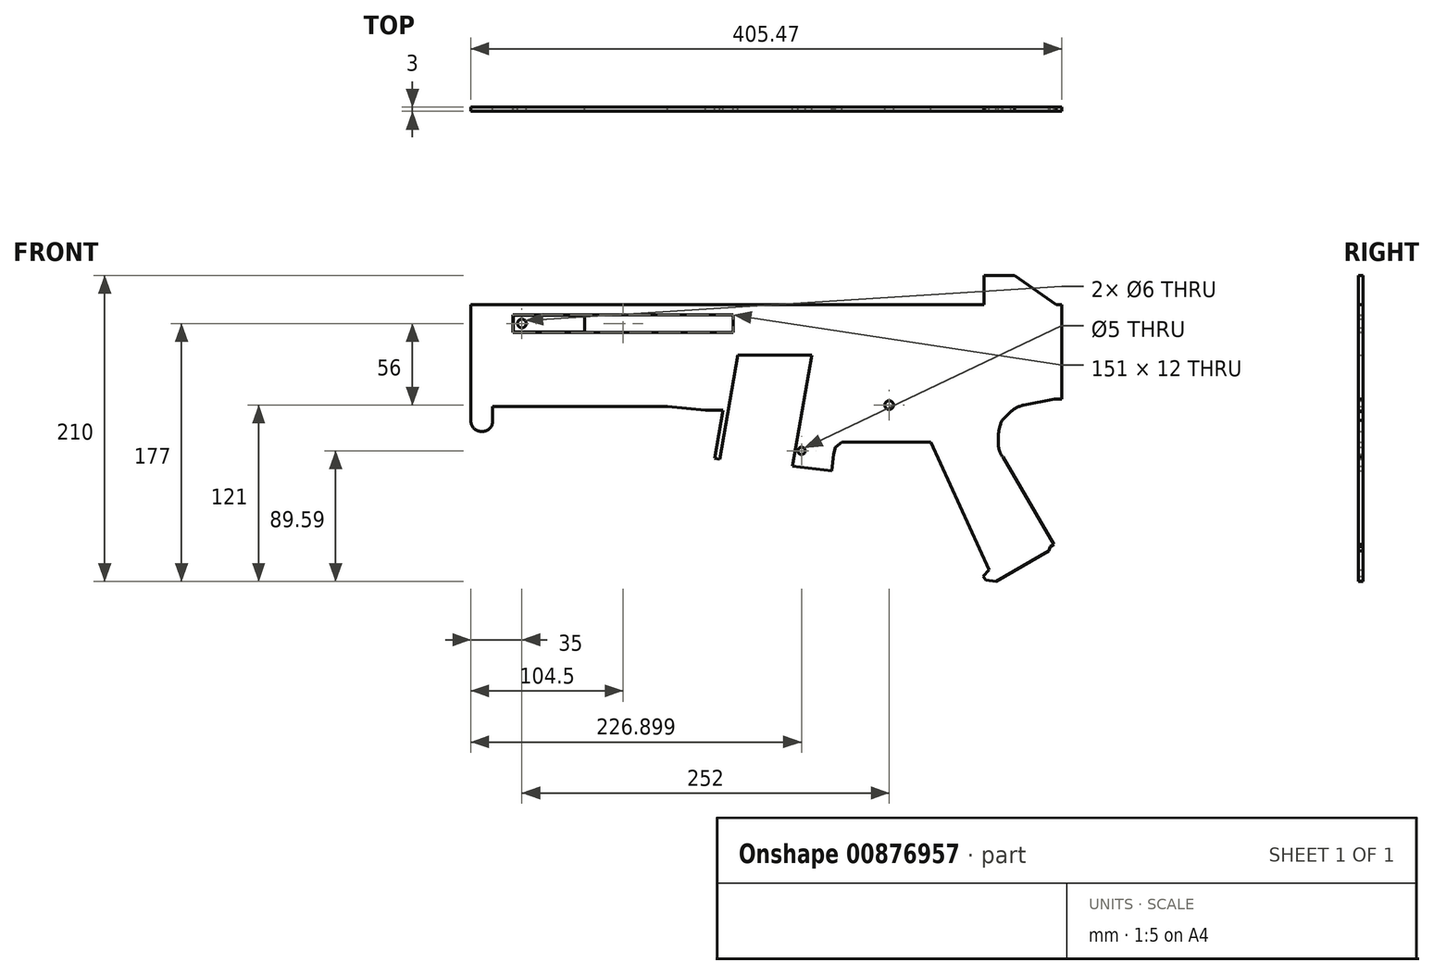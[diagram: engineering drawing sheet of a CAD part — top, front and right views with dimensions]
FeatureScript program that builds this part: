
annotation { "Feature Type Name" : "Feature", "Feature Type Description" : "" }
export const myFeature = defineFeature(function(context is Context, id is Id, definition is map)
    precondition{}
    {
        {
            var Q0;
            Q0=qCreatedBy(makeId("Front.planeOp"),FACE);
            var sketch = newSketch(context, id + "F0", { "sketchPlane" : qUnion([Q0])});
            skLineSegment(sketch, "E0", {"start": v(53.47, -65) * mm, "end": v(53.47, 0) * mm});
            skLineSegment(sketch, "E1", {"start": v(0, 0) * mm, "end": v(-0.03, 20) * mm});
            skLineSegment(sketch, "E2", {"start": v(-0.03, 20) * mm, "end": v(20.97, 20) * mm});
            skPoint(sketch, "E3.visualSharp", {"position": v(-0.03, 20) * mm});
            skPoint(sketch, "E4.visualSharp", {"position": v(20.97, 20) * mm});
            skPoint(sketch, "E5.visualSharp", {"position": v(53.47, 0) * mm});
            skPoint(sketch, "E6.visualSharp", {"position": v(0, 0) * mm});
            skLineSegment(sketch, "E7", {"start": v(53.47, -65) * mm, "end": v(48.47, -65) * mm});
            skLineSegment(sketch, "E8", {"start": v(48.47, -65) * mm, "end": v(27.47, -69) * mm});
            skLineSegment(sketch, "E9", {"start": v(18.47, -73.5) * mm, "end": v(12.47, -79.5) * mm});
            skLineSegment(sketch, "E10", {"start": v(9.97, -90.5) * mm, "end": v(9.97, -96.5) * mm});
            skLineSegment(sketch, "E11", {"start": v(12.97, -104.5) * mm, "end": v(47.97, -164.5) * mm});
            skLineSegment(sketch, "E12", {"start": v(47.97, -164.5) * mm, "end": v(45.47, -166) * mm});
            skLineSegment(sketch, "E13", {"start": v(45.47, -166) * mm, "end": v(44.47, -169) * mm});
            skLineSegment(sketch, "E14", {"start": v(44.47, -169) * mm, "end": v(8.47, -190) * mm});
            skLineSegment(sketch, "E15", {"start": v(8.47, -190) * mm, "end": v(1.47, -189) * mm});
            skLineSegment(sketch, "E16", {"start": v(1.47, -189) * mm, "end": v(-0.53, -186.5) * mm});
            skLineSegment(sketch, "E17", {"start": v(-0.53, -186.5) * mm, "end": v(3.47, -182) * mm});
            skLineSegment(sketch, "E18", {"start": v(3.47, -182) * mm, "end": v(-36.5, -94.5) * mm});
            skArc(sketch, "E19", {"start": v(9.97, -90.5) * mm, "mid": v(10.6, -84.86) * mm, "end": v(12.47, -79.5) * mm});
            skArc(sketch, "E20", {"start": v(27.47, -69) * mm, "mid": v(22.66, -70.63) * mm, "end": v(18.47, -73.5) * mm});
            skArc(sketch, "E21", {"start": v(9.97, -96.5) * mm, "mid": v(10.75, -100.77) * mm, "end": v(12.97, -104.5) * mm});
            skLineSegment(sketch, "E22", {"start": v(0, 0) * mm, "end": v(-352, 0) * mm});
            skLineSegment(sketch, "E23", {"start": v(-345, -87) * mm, "end": v(-344, -87) * mm});
            skLineSegment(sketch, "E24", {"start": v(-337, -80) * mm, "end": v(-337, -70) * mm});
            skLineSegment(sketch, "E25", {"start": v(-337, -70) * mm, "end": v(-217, -70) * mm});
            skLineSegment(sketch, "E26", {"start": v(-217, -70) * mm, "end": v(-191, -72.5) * mm});
            skLineSegment(sketch, "E27", {"start": v(-191, -72.5) * mm, "end": v(-179, -72.5) * mm});
            skLineSegment(sketch, "E28", {"start": v(-179, -72.5) * mm, "end": v(-184.82, -105.5) * mm});
            skLineSegment(sketch, "E29", {"start": v(-352, -80) * mm, "end": v(-352, -55.5) * mm});
            skLineSegment(sketch, "E30", {"start": v(-352, 0) * mm, "end": v(-352, -39) * mm});
            skLineSegment(sketch, "E31", {"start": v(-103, -102.5) * mm, "end": v(-102, -98) * mm});
            skLineSegment(sketch, "E32", {"start": v(-102, -98) * mm, "end": v(-97.5, -94.5) * mm});
            skLineSegment(sketch, "E33", {"start": v(-181.32, -106) * mm, "end": v(-184.82, -105.5) * mm});
            skLineSegment(sketch, "E34", {"start": v(-181.32, -106) * mm, "end": v(-172.41, -55.5) * mm});
            skLineSegment(sketch, "E35", {"start": v(-131.43, -111) * mm, "end": v(-121.64, -55.5) * mm});
            skPoint(sketch, "E36", {"position": v(-317, -13) * mm});
            skPoint(sketch, "E37", {"position": v(-215, -13) * mm});
            skLineSegment(sketch, "E38", {"start": v(-97.5, -94.5) * mm, "end": v(-36.5, -94.5) * mm});
            skPoint(sketch, "E39.visualSharp", {"position": v(-352, -87) * mm});
            skArc(sketch, "E39.filletArc", {"start": v(-352, -80) * mm, "mid": v(-349.95, -84.95) * mm, "end": v(-345, -87) * mm});
            skPoint(sketch, "E40.visualSharp", {"position": v(-337, -87) * mm});
            skArc(sketch, "E40.filletArc", {"start": v(-344, -87) * mm, "mid": v(-339.05, -84.95) * mm, "end": v(-337, -80) * mm});
            skPoint(sketch, "E41", {"position": v(-323, -7) * mm});
            skPoint(sketch, "E42", {"position": v(-209, -7) * mm});
            skLineSegment(sketch, "E43.bottom", {"start": v(-323, -7) * mm, "end": v(-172, -7) * mm});
            skLineSegment(sketch, "E43.top", {"start": v(-323, -19) * mm, "end": v(-172, -19) * mm});
            skLineSegment(sketch, "E43.left", {"start": v(-323, -7) * mm, "end": v(-323, -19) * mm});
            skLineSegment(sketch, "E43.right", {"start": v(-172, -7) * mm, "end": v(-172, -19) * mm});
            skPoint(sketch, "E44", {"position": v(-121.16, -2.5) * mm});
            skLineSegment(sketch, "E45", {"start": v(-118.7, -38.77) * mm, "end": v(-117.99, -34.77) * mm});
            skLineSegment(sketch, "E46", {"start": v(-172.41, -55.5) * mm, "end": v(-168.76, -34.77) * mm});
            skLineSegment(sketch, "E47", {"start": v(-168.76, -34.77) * mm, "end": v(-117.99, -34.77) * mm});
            skLineSegment(sketch, "E48", {"start": v(-121.64, -55.5) * mm, "end": v(-118.7, -38.77) * mm});
            skLineSegment(sketch, "E49", {"start": v(-104.53, -114) * mm, "end": v(-103, -102.5) * mm});
            skLineSegment(sketch, "E50", {"start": v(-352, -39) * mm, "end": v(-352, -55.5) * mm});
            skLineSegment(sketch, "E51", {"start": v(-104.53, -114) * mm, "end": v(-131.43, -111) * mm});
            skCircle(sketch, "E52", {"center": v(-65, -69) * mm, "radius": 3 * mm});
            skCircle(sketch, "E53", {"center": v(-125.1, -100.41) * mm, "radius": 2.5 * mm});
            skLineSegment(sketch, "E54", {"start": v(53.47, 0) * mm, "end": v(49.47, 0) * mm});
            skLineSegment(sketch, "E55", {"start": v(49.47, 0) * mm, "end": v(20.97, 20) * mm});
            skPoint(sketch, "E56", {"position": v(-323, -13) * mm});
            skLineSegment(sketch, "E57.bottom", {"start": v(-322.75, -7.25) * mm, "end": v(-274, -7.25) * mm});
            skLineSegment(sketch, "E57.top", {"start": v(-322.75, -18.75) * mm, "end": v(-274, -18.75) * mm});
            skLineSegment(sketch, "E57.left", {"start": v(-322.75, -7.25) * mm, "end": v(-322.75, -18.75) * mm});
            skLineSegment(sketch, "E57.right", {"start": v(-274, -7.25) * mm, "end": v(-274, -18.75) * mm});
            skCircle(sketch, "E58", {"center": v(-317, -13) * mm, "radius": 3 * mm});
            skPoint(sketch, "E59", {"position": v(-314, -13) * mm});
            skSolve(sketch);
        }
        {
            var Q0;
            Q0=qSketchRegion(id+"F0",true);
            var Q1;
            Q1=makeQuery(id+"F0.imprint","IMPRINT",FACE,{"disambiguationData":[TD([[makeQuery(id+"F0.imprint","IMPRINT",EDGE,{"derivedFrom":sQuery(id+"F0.wireOp",EDGE,"7KHTMWfU-3Zso-w6jU-E75I-gNLATLITgT0v.bottom")}),-1.0]])]});
            var Q2;
            Q2=makeQuery(id+"F0.imprint","IMPRINT",FACE,{"disambiguationData":[TD([[makeQuery(id+"F0.imprint","IMPRINT",EDGE,{"derivedFrom":sQuery(id+"F0.wireOp",EDGE,"h5b3wBjq-2nQV-NM1d-5vbp-s6v93ooiL6zY.bottom")}),-1.0]])]});
            var Q3;
            Q3=makeQuery(id+"F0.imprint","IMPRINT",FACE,{"disambiguationData":[TD([[makeQuery(id+"F0.imprint","IMPRINT",EDGE,{"derivedFrom":sQuery(id+"F0.wireOp",EDGE,"E57.bottom")}),-1.0]])]});
            extrude(context, id + "F1", {"entities" : qUnion([Q0, Q1, Q2, Q3]), "depth" : 3 * mm, "offsetDistance" : 25 * mm});
        }
    });
